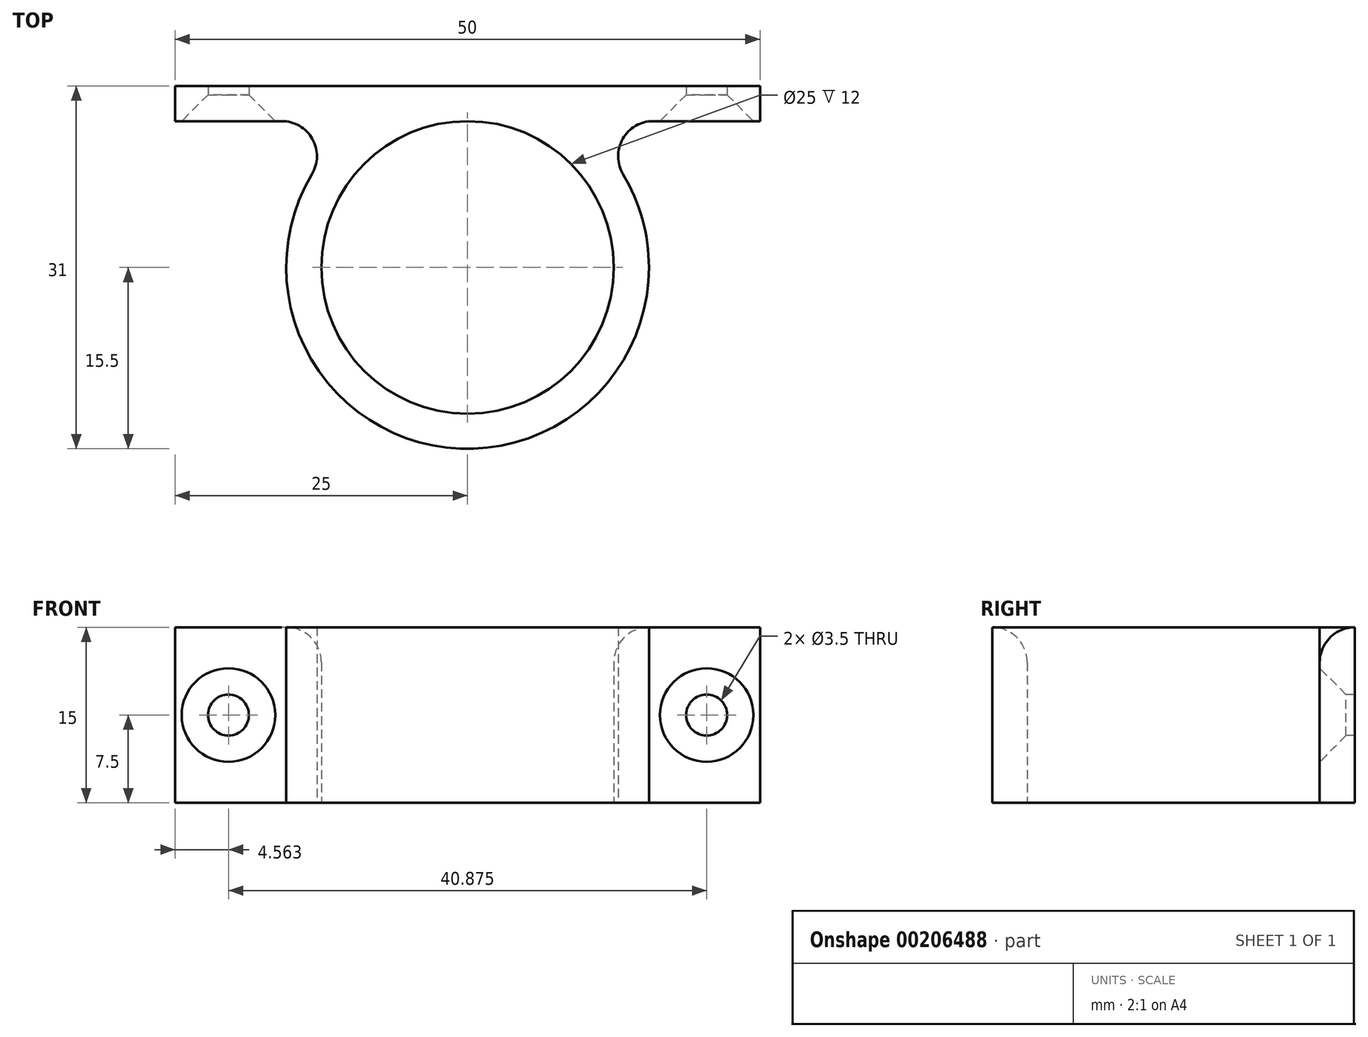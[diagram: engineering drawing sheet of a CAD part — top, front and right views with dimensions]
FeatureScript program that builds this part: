
annotation { "Feature Type Name" : "Feature", "Feature Type Description" : "" }
export const myFeature = defineFeature(function(context is Context, id is Id, definition is map)
    precondition{}
    {
        {
            var Q0;
            Q0=qCreatedBy(makeId("Top.planeOp"),FACE);
            var sketch = newSketch(context, id + "F0", { "sketchPlane" : qUnion([Q0])});
            skCircle(sketch, "E0", {"center": v(0, 0) * mm, "radius": 12.5 * mm});
            skArc(sketch, "E1", {"start": v(-13.3, 7.96) * mm, "mid": v(0, -15.5) * mm, "end": v(13.3, 7.96) * mm});
            skLineSegment(sketch, "E2.bottom", {"start": v(15.87, 12.5) * mm, "end": v(25, 12.5) * mm});
            skLineSegment(sketch, "E2.top", {"start": v(0, 15.5) * mm, "end": v(25, 15.5) * mm});
            skLineSegment(sketch, "E2.right", {"start": v(25, 12.5) * mm, "end": v(25, 15.5) * mm});
            skLineSegment(sketch, "E3.bottom", {"start": v(-15.87, 12.5) * mm, "end": v(-25, 12.5) * mm});
            skLineSegment(sketch, "E3.top", {"start": v(0, 15.5) * mm, "end": v(-25, 15.5) * mm});
            skLineSegment(sketch, "E3.right", {"start": v(-25, 12.5) * mm, "end": v(-25, 15.5) * mm});
            skPoint(sketch, "E3.left.start.orphan", {"position": v(0, 12.5) * mm});
            skPoint(sketch, "E4.visualSharp", {"position": v(-9.17, 12.5) * mm});
            skArc(sketch, "E4.filletArc", {"start": v(-13.3, 7.96) * mm, "mid": v(-13.26, 10.98) * mm, "end": v(-15.87, 12.5) * mm});
            skPoint(sketch, "E5.visualSharp", {"position": v(9.17, 12.5) * mm});
            skArc(sketch, "E5.filletArc", {"start": v(15.87, 12.5) * mm, "mid": v(13.26, 10.98) * mm, "end": v(13.3, 7.96) * mm});
            skSolve(sketch);
        }
        {
            var Q0;
            Q0=makeQuery(id+"F0.imprint","IMPRINT",FACE,{"disambiguationData":[TD([[makeQuery(id+"F0.imprint","IMPRINT",EDGE,{"derivedFrom":sQuery(id+"F0.wireOp",EDGE,"E0")}),-1.0]])]});
            extrude(context, id + "F1", {"entities" : qUnion([Q0]), "depth" : 15 * mm, "offsetDistance" : 25 * mm});
        }
        {
            var Q0;
            Q0=makeQuery(id+"F1.opExtrude","CAP_EDGE",EDGE,{"disambiguationData":[OSD([sQuery(id+"F0.wireOp",EDGE,"E0")])],"isStart":false});
            fillet(context, id + "F2", {"entities" : qUnion([Q0]), "radius" : 3 * mm, "tangentPropagation" : true, "allowEdgeOverflow" : false});
        }
        {
            var Q0;
            Q0=makeQuery(id+"F1.opExtrude","SWEPT_FACE",FACE,{"disambiguationData":[OSD([sQuery(id+"F0.wireOp",EDGE,"E3.bottom")])]});
            var sketch = newSketch(context, id + "F3", { "sketchPlane" : qUnion([Q0])});
            skPoint(sketch, "E6", {"position": v(-20.44, 7.5) * mm});
            skPoint(sketch, "E6.positionSnap0", {"position": v(-25, 7.5) * mm});
            skPoint(sketch, "E6.positionSnap1", {"position": v(-20.44, 15) * mm});
            skSolve(sketch);
        }
        {
            var Q0;
            Q0=makeQuery(id+"F1.opExtrude","SWEPT_FACE",FACE,{"disambiguationData":[OSD([sQuery(id+"F0.wireOp",EDGE,"E2.bottom")])]});
            var sketch = newSketch(context, id + "F4", { "sketchPlane" : qUnion([Q0])});
            skPoint(sketch, "E7", {"position": v(20.44, 7.5) * mm});
            skPoint(sketch, "E7.positionSnap0", {"position": v(20.44, 15) * mm});
            skPoint(sketch, "E7.positionSnap1", {"position": v(25, 7.5) * mm});
            skSolve(sketch);
        }
        {
            var Q0;
            Q0=sQuery(id+"F3.wireOp",VERTEX,"E6");
            var Q1;
            Q1=sQuery(id+"F4.wireOp",VERTEX,"E7");
            var Q2;
            Q2=makeQuery(id+"F1.opExtrude","SWEPT_BODY",BODY,{"disambiguationData":[OSD([sQuery(id+"F0.wireOp",EDGE,"E0"),sQuery(id+"F0.wireOp",EDGE,"E1"),sQuery(id+"F0.wireOp",EDGE,"E2.bottom"),sQuery(id+"F0.wireOp",EDGE,"E2.top"),sQuery(id+"F0.wireOp",EDGE,"E2.right"),sQuery(id+"F0.wireOp",EDGE,"E3.bottom"),sQuery(id+"F0.wireOp",EDGE,"E3.top"),sQuery(id+"F0.wireOp",EDGE,"E3.right"),sQuery(id+"F0.wireOp",EDGE,"E4.filletArc"),sQuery(id+"F0.wireOp",EDGE,"E5.filletArc")])]});
            hole(context, id + "F5", {"style" : HoleStyle.C_SINK, "endStyle" : HoleEndStyle.THROUGH, "holeDiameter" : 3.5 * mm, "cSinkDiameter" : 8 * mm, "cSinkAngle" : 90 * degree, "majorDiameter" : 5 * mm, "isTappedThrough" : true, "tappedDepth" : 12 * mm, "tapClearance" : 3, "locations" : qUnion([Q0, Q1]), "scope" : qUnion([Q2])});
        }
    });
